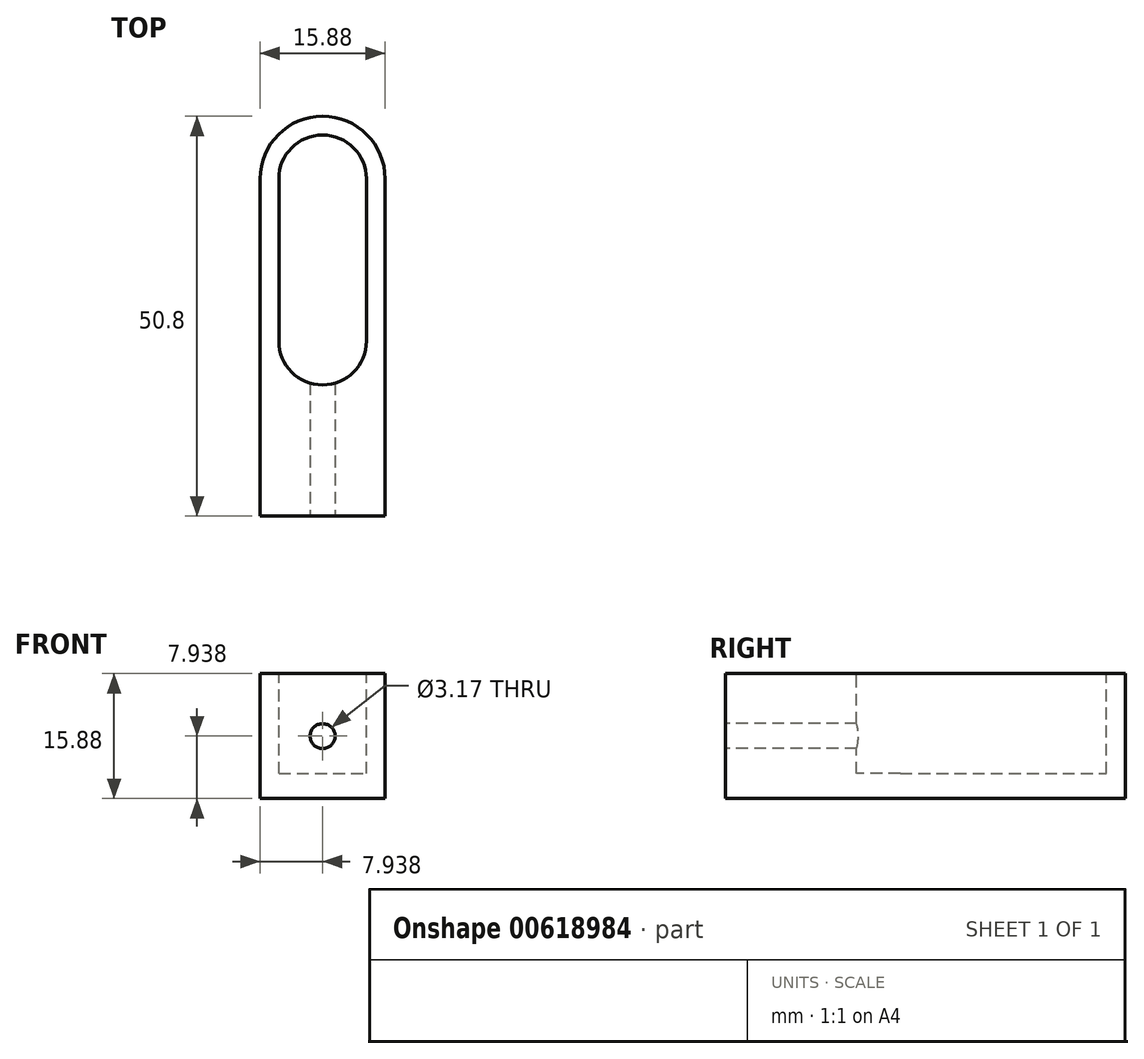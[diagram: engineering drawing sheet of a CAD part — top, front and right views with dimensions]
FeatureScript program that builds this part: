
annotation { "Feature Type Name" : "Feature", "Feature Type Description" : "" }
export const myFeature = defineFeature(function(context is Context, id is Id, definition is map)
    precondition{}
    {
        {
            var Q0;
            Q0=qCreatedBy(makeId("Top.planeOp"),FACE);
            var sketch = newSketch(context, id + "F0", { "sketchPlane" : qUnion([Q0])});
            skLineSegment(sketch, "E0", {"start": v(0, 0) * mm, "end": v(0, 42.86) * mm});
            skLineSegment(sketch, "E1", {"start": v(15.87, 42.86) * mm, "end": v(15.88, 0) * mm});
            skLineSegment(sketch, "E2", {"start": v(15.88, 0) * mm, "end": v(0, 0) * mm});
            skArc(sketch, "E3", {"start": v(15.87, 42.86) * mm, "mid": v(7.94, 50.8) * mm, "end": v(0, 42.86) * mm});
            skSolve(sketch);
        }
        {
            var Q0;
            Q0 = qSketchRegion(id + "F0", true);
            extrude(context, id + "F1", {"entities" : qUnion([Q0]), "depth" : 15.88 * mm, "offsetDistance" : 25.4 * mm});
        }
        {
            var Q0;
            Q0=makeQuery(id+"F1.opExtrude","CAP_FACE",FACE,{"disambiguationData":[OSD([sQuery(id+"F0.wireOp",EDGE,"E0"),sQuery(id+"F0.wireOp",EDGE,"E1"),sQuery(id+"F0.wireOp",EDGE,"E2"),sQuery(id+"F0.wireOp",EDGE,"E3")])],"isStart":false});
            var sketch = newSketch(context, id + "F2", { "sketchPlane" : qUnion([Q0])});
            skLineSegment(sketch, "E4.0", {"start": v(2.38, 22.23) * mm, "end": v(2.38, 42.86) * mm});
            skArc(sketch, "E4.1", {"start": v(13.5, 42.86) * mm, "mid": v(7.94, 48.42) * mm, "end": v(2.38, 42.86) * mm});
            skLineSegment(sketch, "E4.2", {"start": v(13.5, 42.86) * mm, "end": v(13.5, 22.23) * mm});
            skArc(sketch, "E5", {"start": v(2.38, 22.23) * mm, "mid": v(7.94, 16.67) * mm, "end": v(13.5, 22.23) * mm});
            skSolve(sketch);
        }
        {
            var Q0;
            Q0 = qSketchRegion(id + "F2", true);
            extrude(context, id + "F3", {"entities" : qUnion([Q0]), "operationType" : NewBodyOperationType.REMOVE, "oppositeDirection" : true, "depth" : 12.7 * mm, "offsetDistance" : 25.4 * mm});
        }
        {
            var Q0;
            Q0=makeQuery(id+"F1.opExtrude","SWEPT_FACE",FACE,{"disambiguationData":[OSD([sQuery(id+"F0.wireOp",EDGE,"E2")])]});
            var sketch = newSketch(context, id + "F4", { "sketchPlane" : qUnion([Q0])});
            skCircle(sketch, "E6", {"center": v(7.94, 7.94) * mm, "radius": 1.59 * mm});
            skPoint(sketch, "E6.centerSnap0", {"position": v(0, 7.94) * mm});
            skPoint(sketch, "E6.centerSnap1", {"position": v(7.94, 0) * mm});
            skSolve(sketch);
        }
        {
            var Q0;
            Q0 = qSketchRegion(id + "F4", true);
            var Q1;
            Q1=makeQuery(id+"F3.boolean.opBoolean","COPY",FACE,{"derivedFrom":makeQuery(id+"F3.opExtrude","SWEPT_FACE",FACE,{"disambiguationData":[OSD([sQuery(id+"F2.wireOp",EDGE,"E5")])]})});
            extrude(context, id + "F5", {"entities" : qUnion([Q0]), "operationType" : NewBodyOperationType.REMOVE, "endBound" : BoundingType.UP_TO_SURFACE, "oppositeDirection" : true, "depth" : 25.4 * mm, "endBoundEntityFace" : qUnion([Q1]), "offsetDistance" : 25.4 * mm});
        }
    });
